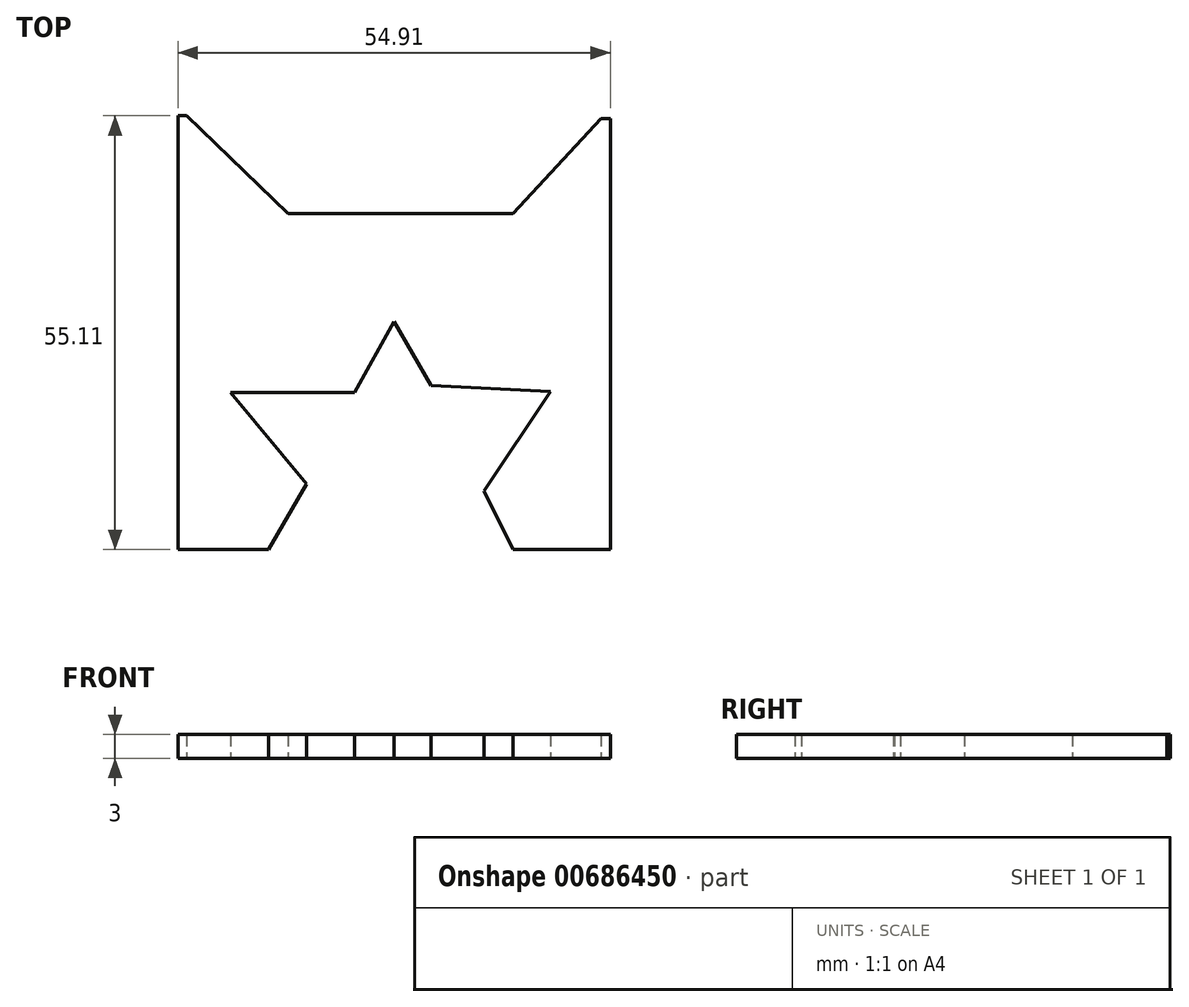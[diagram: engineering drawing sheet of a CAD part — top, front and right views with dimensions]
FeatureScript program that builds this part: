
annotation { "Feature Type Name" : "Feature", "Feature Type Description" : "" }
export const myFeature = defineFeature(function(context is Context, id is Id, definition is map)
    precondition{}
    {
        {
            var Q0;
            Q0=qCreatedBy(makeId("Top.planeOp"),FACE);
            var sketch = newSketch(context, id + "F0", { "sketchPlane" : qUnion([Q0])});
            skLineSegment(sketch, "E0", {"start": v(2.37, -2.36) * mm, "end": v(2.37, -57.47) * mm});
            skLineSegment(sketch, "E1", {"start": v(2.37, -57.47) * mm, "end": v(13.85, -57.47) * mm});
            skLineSegment(sketch, "E2", {"start": v(13.85, -57.47) * mm, "end": v(18.68, -49.17) * mm});
            skLineSegment(sketch, "E3", {"start": v(18.68, -49.17) * mm, "end": v(9.02, -37.49) * mm});
            skLineSegment(sketch, "E4", {"start": v(9.02, -37.49) * mm, "end": v(24.76, -37.49) * mm});
            skLineSegment(sketch, "E5", {"start": v(24.76, -37.49) * mm, "end": v(29.78, -28.51) * mm});
            skLineSegment(sketch, "E6", {"start": v(29.78, -28.51) * mm, "end": v(34.5, -36.62) * mm});
            skLineSegment(sketch, "E7", {"start": v(34.5, -36.62) * mm, "end": v(49.66, -37.4) * mm});
            skLineSegment(sketch, "E8", {"start": v(49.66, -37.4) * mm, "end": v(41.26, -50.03) * mm});
            skLineSegment(sketch, "E9", {"start": v(41.26, -50.03) * mm, "end": v(44.93, -57.47) * mm});
            skLineSegment(sketch, "E10", {"start": v(44.93, -57.47) * mm, "end": v(57.28, -57.47) * mm});
            skLineSegment(sketch, "E11", {"start": v(57.28, -57.47) * mm, "end": v(57.28, -2.74) * mm});
            skLineSegment(sketch, "E12", {"start": v(57.28, -2.74) * mm, "end": v(56.12, -2.74) * mm});
            skLineSegment(sketch, "E13", {"start": v(56.12, -2.74) * mm, "end": v(44.93, -14.8) * mm});
            skLineSegment(sketch, "E14", {"start": v(44.93, -14.8) * mm, "end": v(16.36, -14.8) * mm});
            skLineSegment(sketch, "E15", {"start": v(16.36, -14.8) * mm, "end": v(3.43, -2.36) * mm});
            skLineSegment(sketch, "E16", {"start": v(3.43, -2.36) * mm, "end": v(2.37, -2.36) * mm});
            skSolve(sketch);
        }
        {
            var Q0;
            Q0=makeQuery(id+"F0.imprint","IMPRINT",FACE,{"disambiguationData":[TD([[makeQuery(id+"F0.imprint","IMPRINT",EDGE,{"derivedFrom":sQuery(id+"F0.wireOp",EDGE,"E0")}),1.0]])]});
            extrude(context, id + "F1", {"entities" : qUnion([Q0]), "depth" : 3 * mm, "offsetDistance" : 25 * mm});
        }
    });
